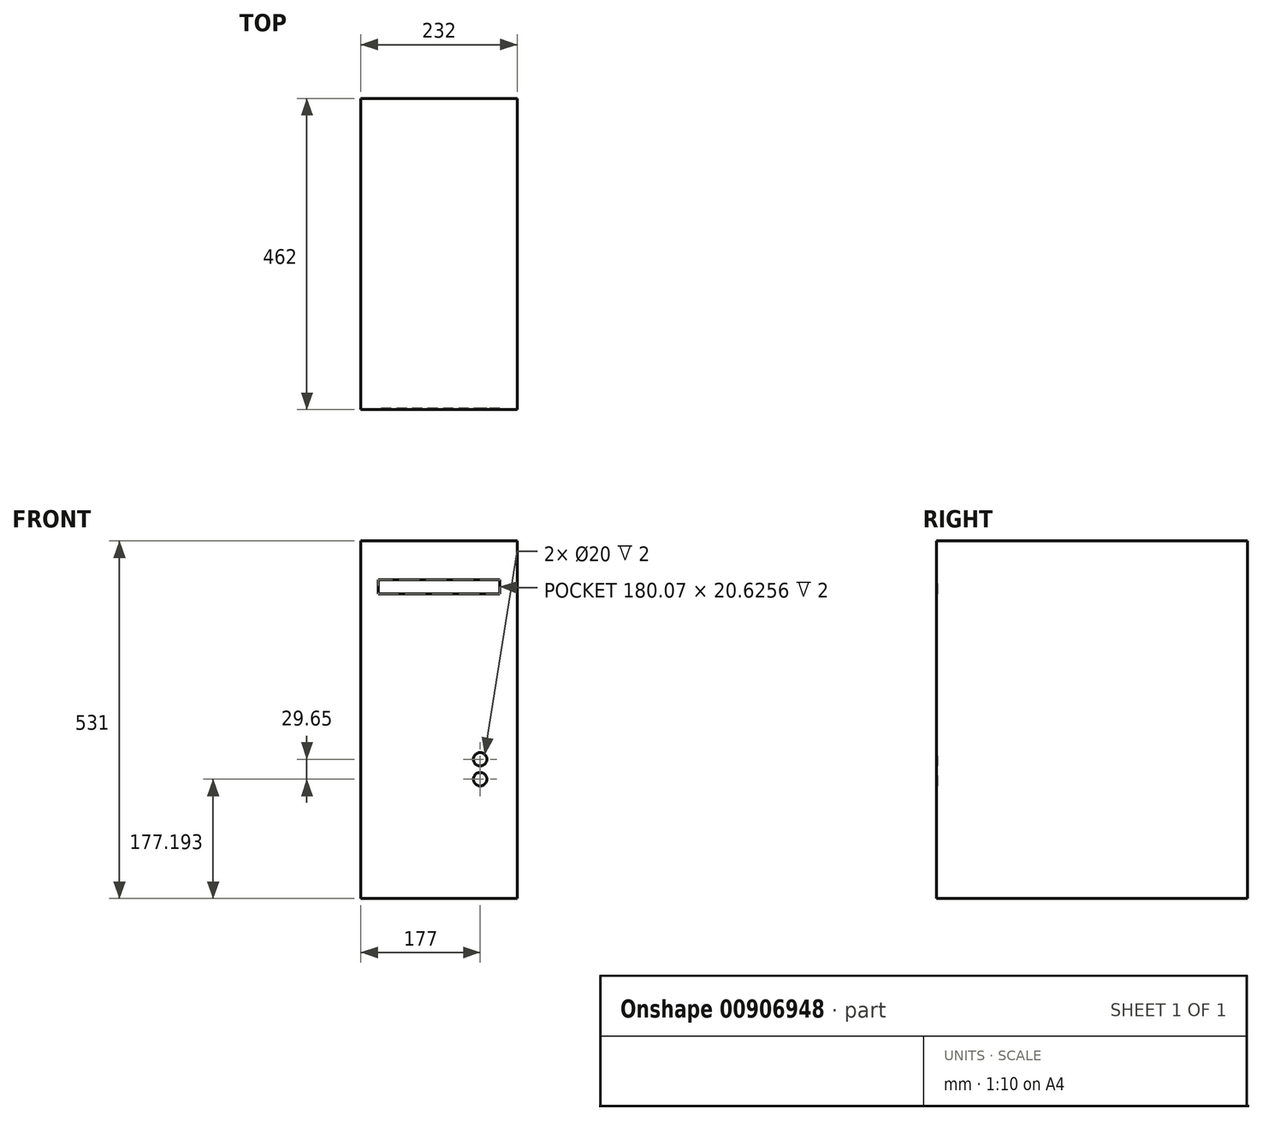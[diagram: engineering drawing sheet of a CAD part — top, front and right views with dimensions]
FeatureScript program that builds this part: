
annotation { "Feature Type Name" : "Feature", "Feature Type Description" : "" }
export const myFeature = defineFeature(function(context is Context, id is Id, definition is map)
    precondition{}
    {
        {
            var Q0;
            Q0=qCreatedBy(makeId("Front.planeOp"),FACE);
            var sketch = newSketch(context, id + "F0", { "sketchPlane" : qUnion([Q0])});
            skLineSegment(sketch, "E0.bottom", {"start": v(0, 0) * mm, "end": v(232, 0) * mm});
            skLineSegment(sketch, "E0.top", {"start": v(0, 531) * mm, "end": v(232, 531) * mm});
            skLineSegment(sketch, "E0.left", {"start": v(0, 0) * mm, "end": v(0, 531) * mm});
            skLineSegment(sketch, "E0.right", {"start": v(232, 0) * mm, "end": v(232, 531) * mm});
            skSolve(sketch);
        }
        {
            var Q0;
            Q0=qSketchRegion(id+"F0",true);
            extrude(context, id + "F1", {"entities" : qUnion([Q0]), "depth" : 462 * mm, "offsetDistance" : 25 * mm});
        }
        {
            var Q0;
            Q0=makeQuery(id+"F1.opExtrude","CAP_FACE",FACE,{"disambiguationData":[OSD([sQuery(id+"F0.wireOp",EDGE,"E0.bottom"),sQuery(id+"F0.wireOp",EDGE,"E0.top"),sQuery(id+"F0.wireOp",EDGE,"E0.left"),sQuery(id+"F0.wireOp",EDGE,"E0.right")])],"isStart":false});
            var sketch = newSketch(context, id + "F2", { "sketchPlane" : qUnion([Q0])});
            skLineSegment(sketch, "E1.bottom", {"start": v(206.03, 452.53) * mm, "end": v(25.97, 452.53) * mm});
            skLineSegment(sketch, "E1.top", {"start": v(206.03, 473.16) * mm, "end": v(25.97, 473.16) * mm});
            skLineSegment(sketch, "E1.left", {"start": v(206.03, 452.53) * mm, "end": v(206.03, 473.16) * mm});
            skLineSegment(sketch, "E1.right", {"start": v(25.97, 452.53) * mm, "end": v(25.97, 473.16) * mm});
            skPoint(sketch, "E1.middle", {"position": v(116, 462.85) * mm});
            skPoint(sketch, "E1.middle.positionSnap0", {"position": v(116, 531) * mm});
            skPoint(sketch, "E1.centerSnap0", {"position": v(116, 531) * mm});
            skCircle(sketch, "E2", {"center": v(177, 206.84) * mm, "radius": 10 * mm});
            skCircle(sketch, "E3", {"center": v(177, 177.2) * mm, "radius": 10 * mm});
            skSolve(sketch);
        }
        {
            var Q0;
            Q0=qSketchRegion(id+"F2",true);
            extrude(context, id + "F3", {"entities" : qUnion([Q0]), "operationType" : NewBodyOperationType.REMOVE, "oppositeDirection" : true, "depth" : 2 * mm, "offsetDistance" : 25 * mm});
        }
    });
